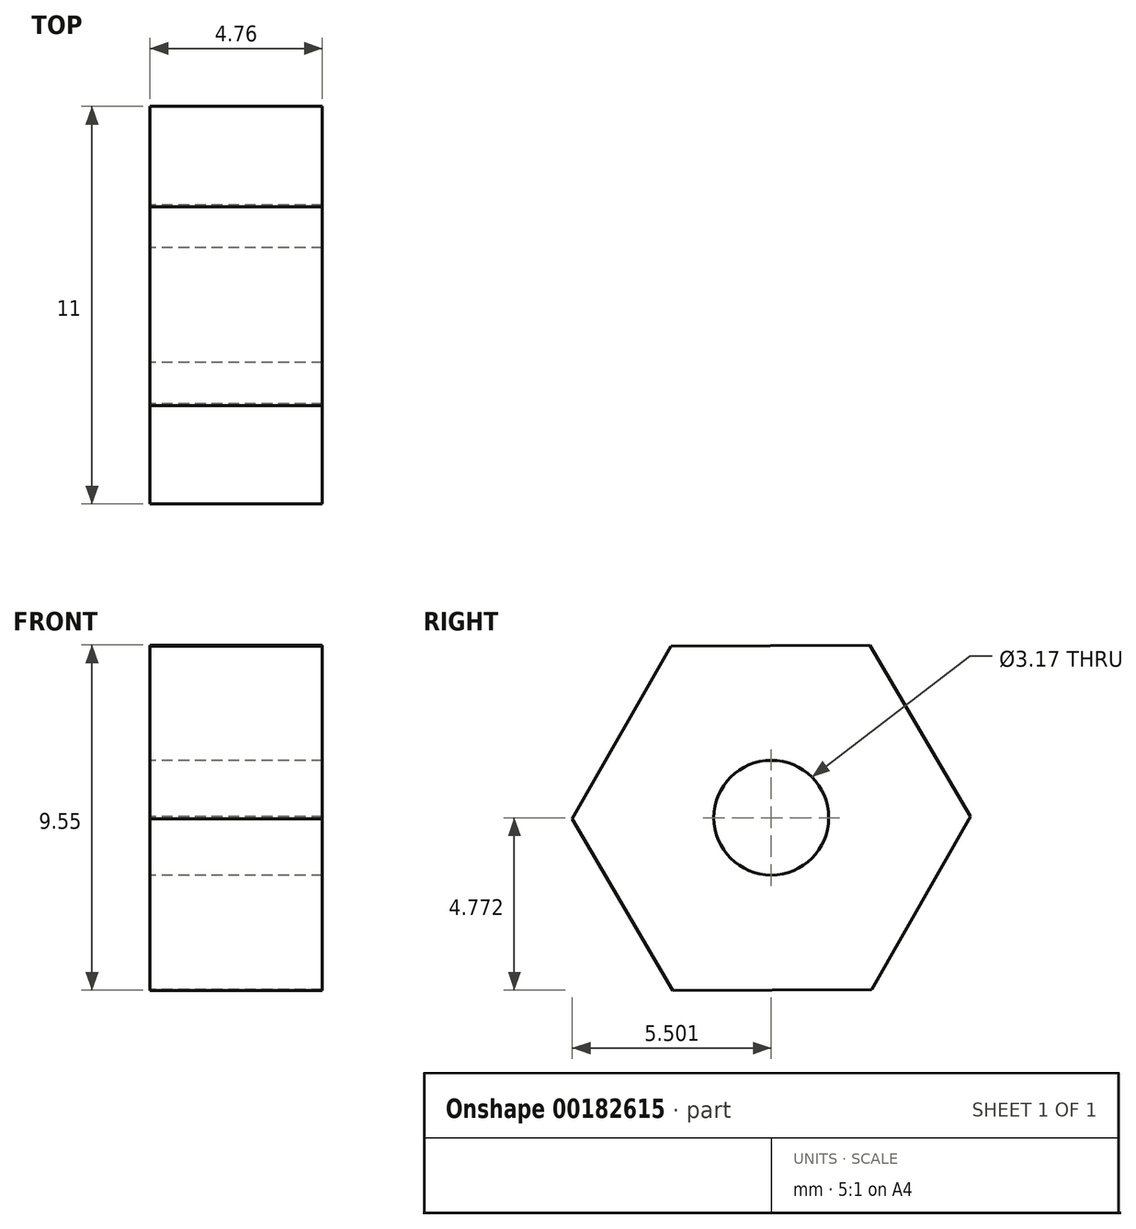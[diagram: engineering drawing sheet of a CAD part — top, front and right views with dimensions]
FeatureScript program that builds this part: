
annotation { "Feature Type Name" : "Feature", "Feature Type Description" : "" }
export const myFeature = defineFeature(function(context is Context, id is Id, definition is map)
    precondition{}
    {
        {
            var Q0;
            Q0=qCreatedBy(makeId("Right.planeOp"),FACE);
            var sketch = newSketch(context, id + "F0", { "sketchPlane" : qUnion([Q0])});
            skCircle(sketch, "E0.cCircle", {"center": v(9.77, 5.72) * mm, "radius": 4.76 * mm, "construction": true});
            skLineSegment(sketch, "E0.0", {"start": v(7.04, 0.95) * mm, "end": v(4.27, 5.7) * mm});
            skLineSegment(sketch, "E0.1", {"start": v(4.27, 5.7) * mm, "end": v(7, 10.47) * mm});
            skLineSegment(sketch, "E0.2", {"start": v(7, 10.47) * mm, "end": v(12.5, 10.5) * mm});
            skLineSegment(sketch, "E0.3", {"start": v(12.5, 10.5) * mm, "end": v(15.27, 5.75) * mm});
            skLineSegment(sketch, "E0.4", {"start": v(15.27, 5.75) * mm, "end": v(12.54, 0.97) * mm});
            skLineSegment(sketch, "E0.5", {"start": v(12.54, 0.97) * mm, "end": v(7.04, 0.95) * mm});
            skPoint(sketch, "E0.0.midPoint", {"position": v(5.66, 3.32) * mm});
            skCircle(sketch, "E1", {"center": v(9.77, 5.72) * mm, "radius": 1.59 * mm});
            skSolve(sketch);
        }
        {
            var Q0;
            Q0 = qSketchRegion(id + "F0", true);
            extrude(context, id + "F1", {"entities" : qUnion([Q0]), "depth" : 4.76 * mm});
        }
    });
